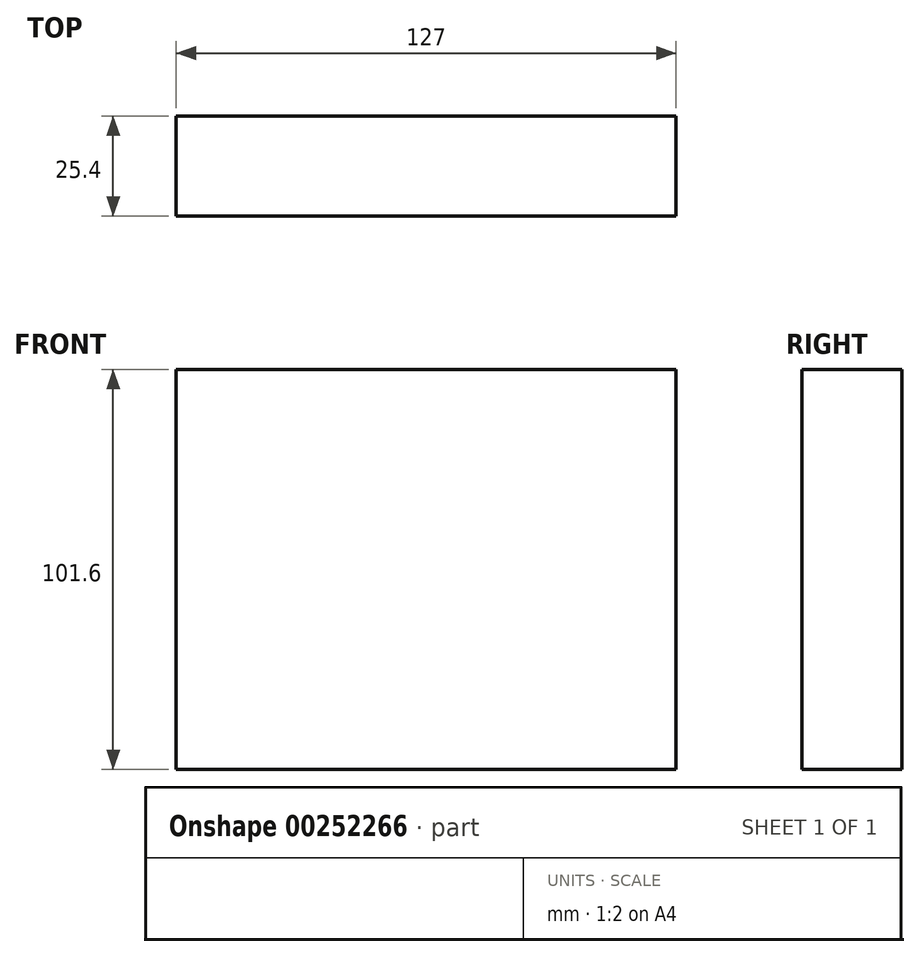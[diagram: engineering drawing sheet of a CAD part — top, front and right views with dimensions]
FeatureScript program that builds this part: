
annotation { "Feature Type Name" : "Feature", "Feature Type Description" : "" }
export const myFeature = defineFeature(function(context is Context, id is Id, definition is map)
    precondition{}
    {
        {
            var Q0;
            Q0=qCreatedBy(makeId("Front.planeOp"),FACE);
            var sketch = newSketch(context, id + "F0", { "sketchPlane" : qUnion([Q0])});
            skLineSegment(sketch, "E0.bottom", {"start": v(63.5, 50.8) * mm, "end": v(-63.5, 50.8) * mm});
            skLineSegment(sketch, "E0.top", {"start": v(63.5, -50.8) * mm, "end": v(-63.5, -50.8) * mm});
            skLineSegment(sketch, "E0.left", {"start": v(63.5, 50.8) * mm, "end": v(63.5, -50.8) * mm});
            skLineSegment(sketch, "E0.right", {"start": v(-63.5, 50.8) * mm, "end": v(-63.5, -50.8) * mm});
            skPoint(sketch, "E0.middle", {"position": v(0, 0) * mm});
            skSolve(sketch);
        }
        {
            var Q0;
            Q0=makeQuery(id+"F0.imprint","IMPRINT",FACE,{"disambiguationData":[TD([[makeQuery(id+"F0.imprint","IMPRINT",EDGE,{"derivedFrom":sQuery(id+"F0.wireOp",EDGE,"E0.bottom")}),1.0]])]});
            extrude(context, id + "F1", {"entities" : qUnion([Q0]), "depth" : 25.4 * mm});
        }
    });
